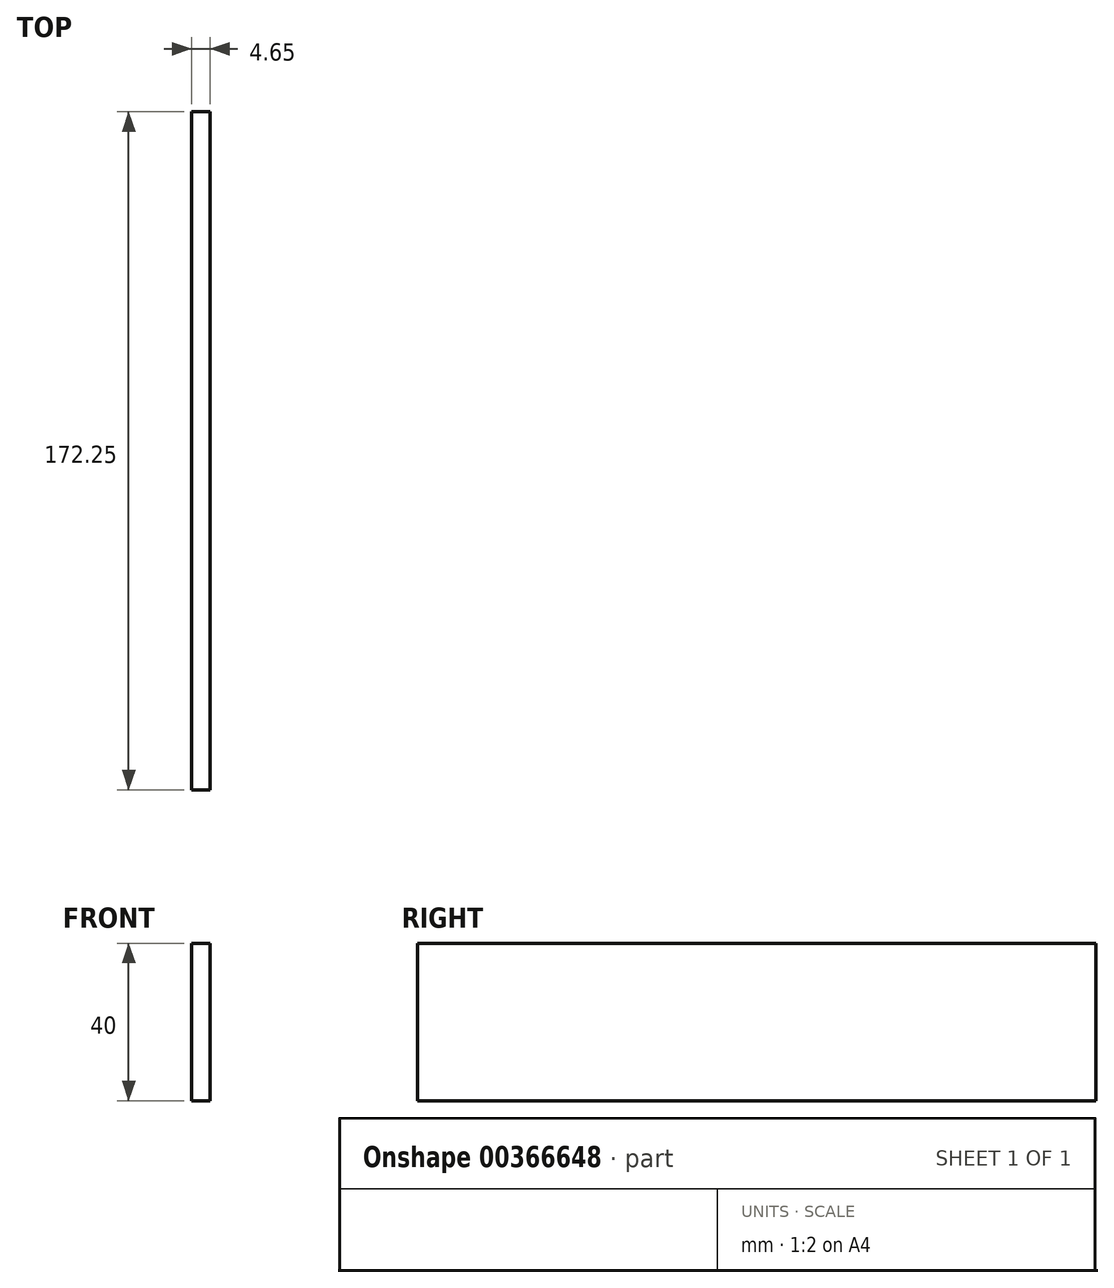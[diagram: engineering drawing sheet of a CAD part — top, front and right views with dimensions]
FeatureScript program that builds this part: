
annotation { "Feature Type Name" : "Feature", "Feature Type Description" : "" }
export const myFeature = defineFeature(function(context is Context, id is Id, definition is map)
    precondition{}
    {
        {
            var Q0;
            Q0=qCreatedBy(makeId("Top.planeOp"),FACE);
            var sketch = newSketch(context, id + "F0", { "sketchPlane" : qUnion([Q0])});
            skLineSegment(sketch, "E0.bottom", {"start": v(-27.33, -75.34) * mm, "end": v(-22.68, -75.34) * mm});
            skLineSegment(sketch, "E0.top", {"start": v(-27.33, 96.9) * mm, "end": v(-22.68, 96.9) * mm});
            skLineSegment(sketch, "E0.left", {"start": v(-27.33, -75.34) * mm, "end": v(-27.33, 96.9) * mm});
            skLineSegment(sketch, "E0.right", {"start": v(-22.68, -75.34) * mm, "end": v(-22.68, 96.9) * mm});
            skSolve(sketch);
        }
        {
            var Q0;
            Q0=makeQuery(id+"F0.imprint","IMPRINT",FACE,{"disambiguationData":[TD([[makeQuery(id+"F0.imprint","IMPRINT",EDGE,{"derivedFrom":sQuery(id+"F0.wireOp",EDGE,"E0.bottom")}),1.0]])]});
            extrude(context, id + "F1", {"entities" : qUnion([Q0]), "depth" : 40 * mm});
        }
    });
